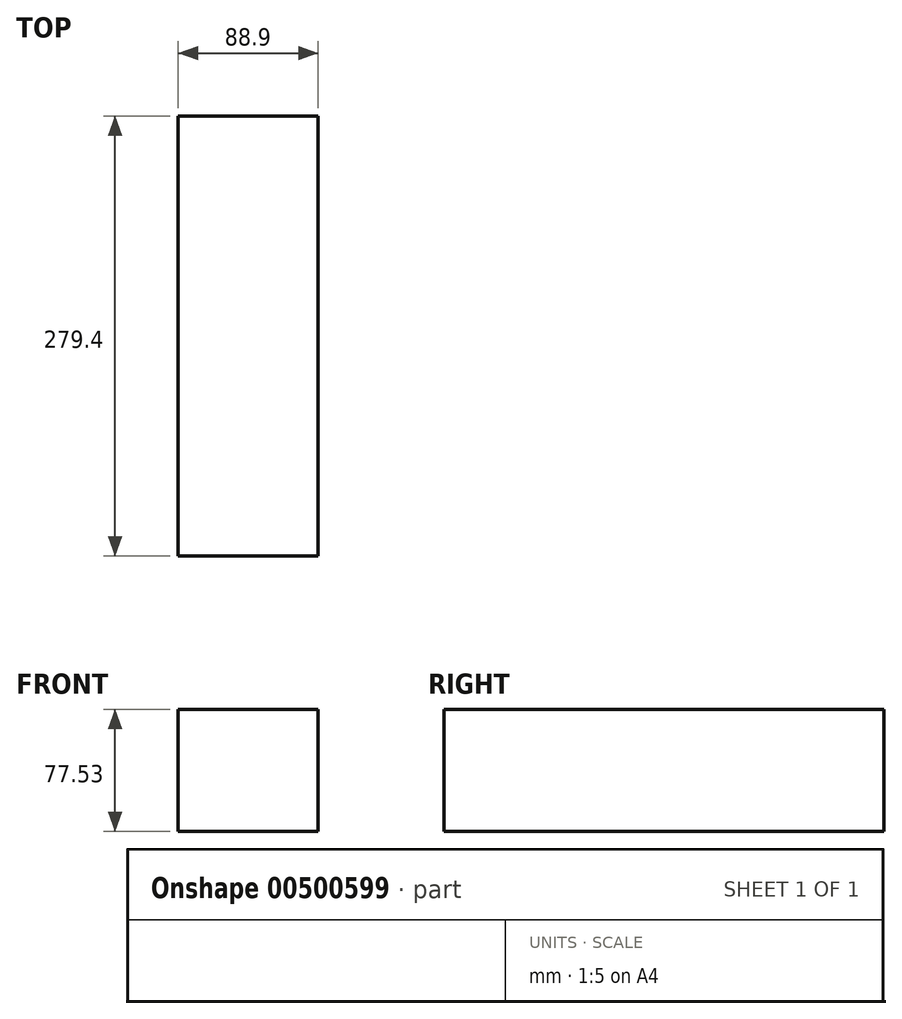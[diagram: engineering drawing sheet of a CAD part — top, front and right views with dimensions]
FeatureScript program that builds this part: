
annotation { "Feature Type Name" : "Feature", "Feature Type Description" : "" }
export const myFeature = defineFeature(function(context is Context, id is Id, definition is map)
    precondition{}
    {
        {
            var Q0;
            Q0=qCreatedBy(makeId("Front.planeOp"),FACE);
            var sketch = newSketch(context, id + "F0", { "sketchPlane" : qUnion([Q0])});
            skLineSegment(sketch, "E0.bottom", {"start": v(-40.22, 34.83) * mm, "end": v(48.68, 34.83) * mm});
            skLineSegment(sketch, "E0.top", {"start": v(-40.22, -42.7) * mm, "end": v(48.68, -42.7) * mm});
            skLineSegment(sketch, "E0.left", {"start": v(-40.22, 34.83) * mm, "end": v(-40.22, -42.7) * mm});
            skLineSegment(sketch, "E0.right", {"start": v(48.68, 34.83) * mm, "end": v(48.68, -42.7) * mm});
            skSolve(sketch);
        }
        {
            var Q0;
            Q0=makeQuery(id+"F0.imprint","IMPRINT",FACE,{"disambiguationData":[TD([[makeQuery(id+"F0.imprint","IMPRINT",EDGE,{"derivedFrom":sQuery(id+"F0.wireOp",EDGE,"E0.bottom")}),-1.0]])]});
            extrude(context, id + "F1", {"entities" : qUnion([Q0]), "depth" : 279.4 * mm});
        }
    });
